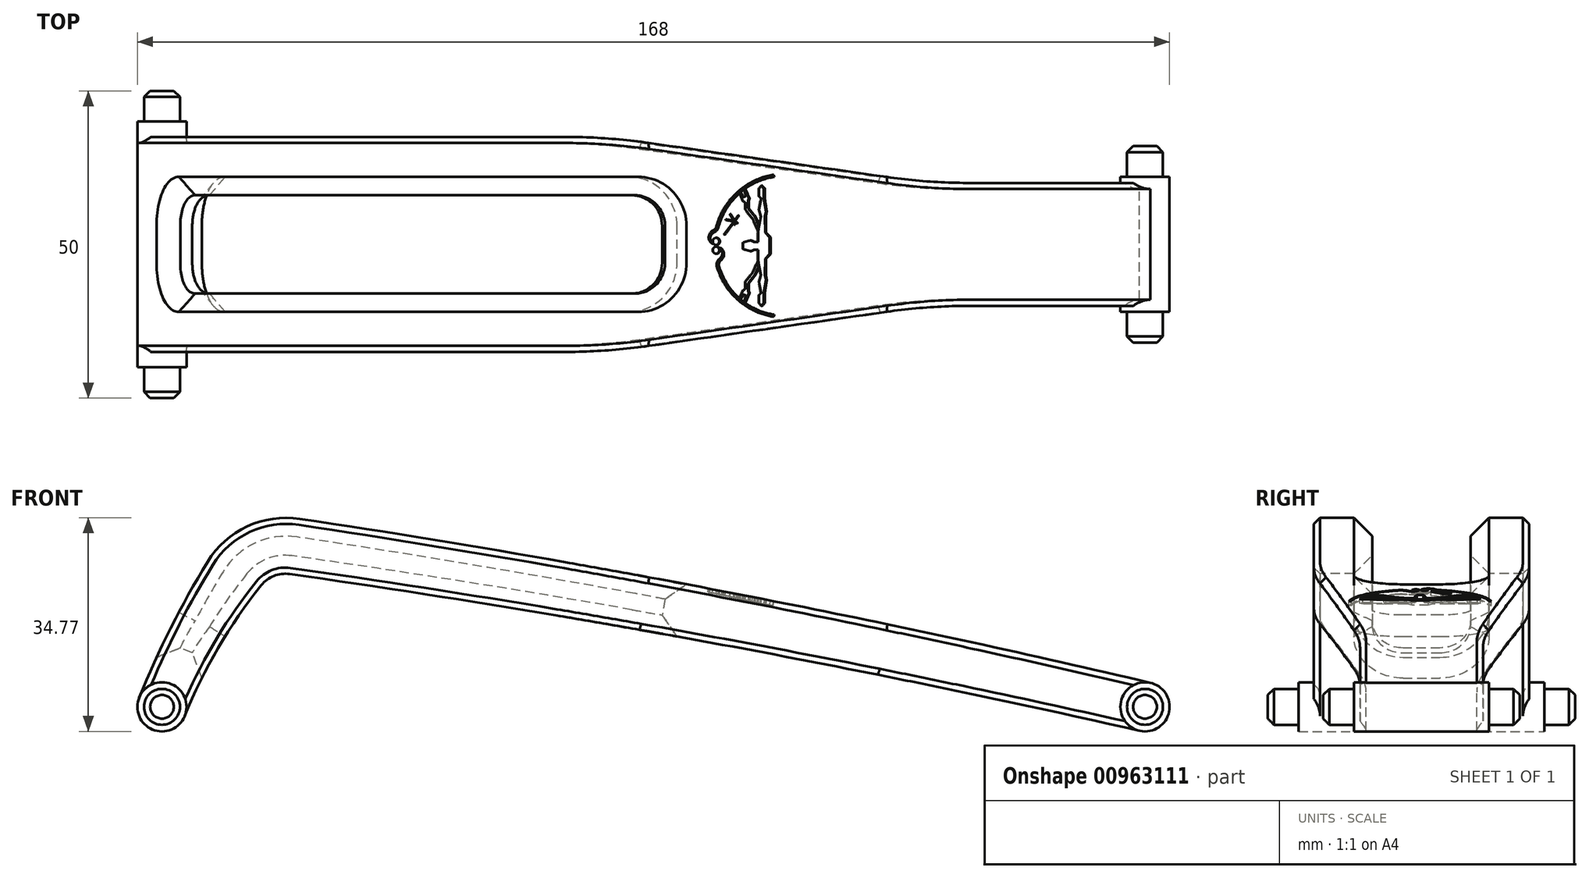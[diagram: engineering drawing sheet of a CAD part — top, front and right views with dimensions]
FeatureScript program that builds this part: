
annotation { "Feature Type Name" : "Feature", "Feature Type Description" : "" }
export const myFeature = defineFeature(function(context is Context, id is Id, definition is map)
    precondition{}
    {
        {
            var Q0;
            Q0=qCreatedBy(makeId("Front.planeOp"),FACE);
            var sketch = newSketch(context, id + "F0", { "sketchPlane" : qUnion([Q0])});
            skCircle(sketch, "E0", {"center": v(0, 0) * mm, "radius": 2.93 * mm});
            skSolve(sketch);
        }
        {
            var Q0;
            Q0 = qSketchRegion(id + "F0", true);
            extrude(context, id + "F1", {"entities" : qUnion([Q0]), "depth" : (22 + 10) * mm, "offsetDistance" : 25 * mm, "symmetric" : true});
        }
        {
            var Q0;
            Q0=qCreatedBy(makeId("Front.planeOp"),FACE);
            var sketch = newSketch(context, id + "F2", { "sketchPlane" : qUnion([Q0])});
            skCircle(sketch, "E1", {"center": v(-160, 0) * mm, "radius": 2.93 * mm});
            skSolve(sketch);
        }
        {
            var Q0;
            Q0 = qSketchRegion(id + "F2", true);
            extrude(context, id + "F3", {"entities" : qUnion([Q0]), "depth" : 50 * mm, "offsetDistance" : 25 * mm, "symmetric" : true});
        }
        {
            var Q0;
            Q0=qCreatedBy(makeId("Front.planeOp"),FACE);
            var sketch = newSketch(context, id + "F4", { "sketchPlane" : qUnion([Q0])});
            skCircle(sketch, "E2", {"center": v(0, 0) * mm, "radius": 4 * mm});
            skSolve(sketch);
        }
        {
            var Q0;
            Q0 = qSketchRegion(id + "F4", true);
            extrude(context, id + "F5", {"entities" : qUnion([Q0]), "operationType" : NewBodyOperationType.ADD, "depth" : (32 - 3 - 7) * mm, "offsetDistance" : 25 * mm, "symmetric" : true});
        }
        {
            var Q0;
            Q0=qCreatedBy(makeId("Front.planeOp"),FACE);
            var sketch = newSketch(context, id + "F6", { "sketchPlane" : qUnion([Q0])});
            skCircle(sketch, "E3", {"center": v(-160, 0) * mm, "radius": 4 * mm});
            skSolve(sketch);
        }
        {
            var Q0;
            Q0 = qSketchRegion(id + "F6", true);
            extrude(context, id + "F7", {"entities" : qUnion([Q0]), "operationType" : NewBodyOperationType.ADD, "depth" : (50 - 3 - 7) * mm, "offsetDistance" : 25 * mm, "symmetric" : true});
        }
        {
            var Q0;
            Q0=qCreatedBy(makeId("Front.planeOp"),FACE);
            var sketch = newSketch(context, id + "F8", { "sketchPlane" : qUnion([Q0])});
            skLineSegment(sketch, "E4", {"start": v(-0.83, -3.91) * mm, "end": v(0.83, 3.91) * mm});
            skLineSegment(sketch, "E5", {"start": v(0.83, 3.91) * mm, "end": v(-149.8, 35.93) * mm, "construction": true});
            skLineSegment(sketch, "E6", {"start": v(-163.7, 1.5) * mm, "end": v(-149.8, 35.93) * mm, "construction": true});
            skLineSegment(sketch, "E7", {"start": v(-156.3, -1.5) * mm, "end": v(-163.7, 1.5) * mm});
            skLineSegment(sketch, "E8", {"start": v(-144.9, 26.7) * mm, "end": v(-156.3, -1.5) * mm, "construction": true});
            skLineSegment(sketch, "E9", {"start": v(-144.9, 26.7) * mm, "end": v(-0.83, -3.91) * mm, "construction": true});
            skPoint(sketch, "E10", {"position": v(-160, 0) * mm});
            skLineSegment(sketch, "E11", {"start": v(-160, 0) * mm, "end": v(0, 0) * mm, "construction": true});
            skArc(sketch, "E12", {"start": v(-142, 22) * mm, "mid": v(-150.1, 10.83) * mm, "end": v(-156.3, -1.5) * mm});
            skArc(sketch, "E13", {"start": v(-0.83, -3.91) * mm, "mid": v(-71.14, 10.53) * mm, "end": v(-142, 22) * mm});
            skArc(sketch, "E14", {"start": v(-147.04, 32) * mm, "mid": v(-156.26, 17.23) * mm, "end": v(-163.7, 1.5) * mm});
            skArc(sketch, "E15", {"start": v(0.83, 3.91) * mm, "mid": v(-72.8, 19.6) * mm, "end": v(-147.04, 32) * mm});
            skSolve(sketch);
        }
        {
            var Q0;
            Q0 = qSketchRegion(id + "F8", true);
            extrude(context, id + "F9", {"entities" : qUnion([Q0]), "depth" : 20 * mm, "offsetDistance" : 25 * mm, "symmetric" : true});
        }
        {
            var Q0;
            Q0=makeQuery(id+"F9.opExtrude","SWEPT_BODY",BODY,{"disambiguationData":[OSD([sQuery(id+"F8.wireOp",EDGE,"E4"),sQuery(id+"F8.wireOp",EDGE,"E5"),sQuery(id+"F8.wireOp",EDGE,"E6"),sQuery(id+"F8.wireOp",EDGE,"E7"),sQuery(id+"F8.wireOp",EDGE,"E8"),sQuery(id+"F8.wireOp",EDGE,"E9")])]});
            var Q1;
            Q1=makeQuery(id+"F3.opExtrude","SWEPT_BODY",BODY,{"disambiguationData":[OSD([sQuery(id+"F2.wireOp",EDGE,"E1")])]});
            var Q2;
            Q2=makeQuery(id+"F1.opExtrude","SWEPT_BODY",BODY,{"disambiguationData":[OSD([sQuery(id+"F0.wireOp",EDGE,"E0")])]});
            booleanBodies(context, id + "F10", {"operationType" : BooleanOperationType.UNION, "tools" : qUnion([Q0, Q1, Q2])});
        }
        {
            var Q0;
            Q0=qCreatedBy(makeId("Front.planeOp"),FACE);
            var sketch = newSketch(context, id + "F11", { "sketchPlane" : qUnion([Q0])});
            skLineSegment(sketch, "E16", {"start": v(-163.7, 1.5) * mm, "end": v(-156.3, -1.5) * mm});
            skLineSegment(sketch, "E17", {"start": v(-88.98, 13.71) * mm, "end": v(-87.43, 22.3) * mm});
            skLineSegment(sketch, "E18", {"start": v(-87.43, 22.3) * mm, "end": v(-187.46, 40.4) * mm, "construction": true});
            skArc(sketch, "E19.0", {"start": v(-87.43, 22.3) * mm, "mid": v(-117.2, 27.42) * mm, "end": v(-147.04, 32) * mm});
            skArc(sketch, "E19.1", {"start": v(-88.98, 13.71) * mm, "mid": v(-115.46, 18.06) * mm, "end": v(-142, 22) * mm});
            skArc(sketch, "E19.2", {"start": v(-142, 22) * mm, "mid": v(-150.1, 10.83) * mm, "end": v(-156.3, -1.5) * mm});
            skArc(sketch, "E19.3", {"start": v(-147.04, 32) * mm, "mid": v(-156.26, 17.23) * mm, "end": v(-163.7, 1.5) * mm});
            skPoint(sketch, "E20.orphan", {"position": v(0.83, 3.91) * mm});
            skPoint(sketch, "E21.orphan", {"position": v(-0.94, -3.89) * mm});
            skSolve(sketch);
        }
        {
            var Q0;
            Q0 = qSketchRegion(id + "F11", true);
            extrude(context, id + "F12", {"entities" : qUnion([Q0]), "operationType" : NewBodyOperationType.ADD, "depth" : 35 * mm, "offsetDistance" : 25 * mm, "symmetric" : true});
        }
        {
            var Q0;
            Q0=makeQuery(id+"F12.boolean.opBoolean","INTERSECT",EDGE,{"derivedFrom":[makeQuery(id+"F9.opExtrude","CAP_FACE",FACE,{"disambiguationData":[OSD([sQuery(id+"F8.wireOp",EDGE,"E4"),sQuery(id+"F8.wireOp",EDGE,"E5"),sQuery(id+"F8.wireOp",EDGE,"E6"),sQuery(id+"F8.wireOp",EDGE,"E7"),sQuery(id+"F8.wireOp",EDGE,"E8"),sQuery(id+"F8.wireOp",EDGE,"E9")])],"isStart":true}),makeQuery(id+"F12.opExtrude","SWEPT_FACE",FACE,{"disambiguationData":[OSD([sQuery(id+"F11.wireOp",EDGE,"E17")])]})]});
            chamfer(context, id + "F13", {"entities" : qUnion([Q0]), "chamferType" : ChamferType.OFFSET_ANGLE, "width" : 7.5 * mm, "oppositeDirection" : false, "angle" : 82 * degree, "tangentPropagation" : true});
        }
        {
            var Q0;
            Q0=makeQuery(id+"F12.boolean.opBoolean","INTERSECT",EDGE,{"derivedFrom":[makeQuery(id+"F9.opExtrude","CAP_FACE",FACE,{"disambiguationData":[OSD([sQuery(id+"F8.wireOp",EDGE,"E4"),sQuery(id+"F8.wireOp",EDGE,"E5"),sQuery(id+"F8.wireOp",EDGE,"E6"),sQuery(id+"F8.wireOp",EDGE,"E7"),sQuery(id+"F8.wireOp",EDGE,"E8"),sQuery(id+"F8.wireOp",EDGE,"E9")])],"isStart":false}),makeQuery(id+"F12.opExtrude","SWEPT_FACE",FACE,{"disambiguationData":[OSD([sQuery(id+"F11.wireOp",EDGE,"E17")])]})]});
            chamfer(context, id + "F14", {"entities" : qUnion([Q0]), "chamferType" : ChamferType.OFFSET_ANGLE, "width" : 7.5 * mm, "oppositeDirection" : true, "angle" : 82 * degree, "tangentPropagation" : true});
        }
        {
            var Q0;
            {var subQ0=makeQuery(id+"F9.opExtrude","CAP_FACE",FACE,{"disambiguationData":[OSD([sQuery(id+"F8.wireOp",EDGE,"E4"),sQuery(id+"F8.wireOp",EDGE,"E5"),sQuery(id+"F8.wireOp",EDGE,"E6"),sQuery(id+"F8.wireOp",EDGE,"E7"),sQuery(id+"F8.wireOp",EDGE,"E8"),sQuery(id+"F8.wireOp",EDGE,"E9")])],"isStart":true});Q0=makeQuery(id+"F13.opChamfer","BLEND_EDGE",EDGE,{"blendedFrom":[makeQuery(id+"F12.boolean.opBoolean","INTERSECT",EDGE,{"derivedFrom":[subQ0,makeQuery(id+"F12.opExtrude","SWEPT_FACE",FACE,{"disambiguationData":[OSD([sQuery(id+"F11.wireOp",EDGE,"E17")])]})]}),subQ0],"blendedInto":[subQ0]});}
            var Q1;
            {var subQ0=sQuery(id+"F11.wireOp",EDGE,"E17");Q1=makeQuery(id+"F13.opChamfer","BLEND_EDGE",EDGE,{"blendedFrom":[makeQuery(id+"F12.boolean.opBoolean","INTERSECT",EDGE,{"derivedFrom":[makeQuery(id+"F9.opExtrude","CAP_FACE",FACE,{"disambiguationData":[OSD([sQuery(id+"F8.wireOp",EDGE,"E4"),sQuery(id+"F8.wireOp",EDGE,"E5"),sQuery(id+"F8.wireOp",EDGE,"E6"),sQuery(id+"F8.wireOp",EDGE,"E7"),sQuery(id+"F8.wireOp",EDGE,"E8"),sQuery(id+"F8.wireOp",EDGE,"E9")])],"isStart":true}),makeQuery(id+"F12.opExtrude","SWEPT_FACE",FACE,{"disambiguationData":[OSD([subQ0])]})]}),makeQuery(id+"F12.opExtrude","CAP_FACE",FACE,{"disambiguationData":[OSD([sQuery(id+"F11.wireOp",EDGE,"2c269e23-bd51-4eb5-b0e0-de77504a2cef.0"),sQuery(id+"F11.wireOp",EDGE,"2c269e23-bd51-4eb5-b0e0-de77504a2cef.2"),sQuery(id+"F11.wireOp",EDGE,"2c269e23-bd51-4eb5-b0e0-de77504a2cef.3"),sQuery(id+"F11.wireOp",EDGE,"2c269e23-bd51-4eb5-b0e0-de77504a2cef.4"),sQuery(id+"F11.wireOp",EDGE,"E16"),subQ0])],"isStart":true})],"blendedInto":[makeQuery(id+"F12.opExtrude","CAP_FACE",FACE,{"disambiguationData":[OSD([sQuery(id+"F11.wireOp",EDGE,"2c269e23-bd51-4eb5-b0e0-de77504a2cef.0"),sQuery(id+"F11.wireOp",EDGE,"2c269e23-bd51-4eb5-b0e0-de77504a2cef.2"),sQuery(id+"F11.wireOp",EDGE,"2c269e23-bd51-4eb5-b0e0-de77504a2cef.3"),sQuery(id+"F11.wireOp",EDGE,"2c269e23-bd51-4eb5-b0e0-de77504a2cef.4"),sQuery(id+"F11.wireOp",EDGE,"E16"),subQ0])],"isStart":true})]});}
            var Q2;
            {var subQ0=sQuery(id+"F11.wireOp",EDGE,"E17");Q2=makeQuery(id+"F14.opChamfer","BLEND_EDGE",EDGE,{"blendedFrom":[makeQuery(id+"F12.boolean.opBoolean","INTERSECT",EDGE,{"derivedFrom":[makeQuery(id+"F9.opExtrude","CAP_FACE",FACE,{"disambiguationData":[OSD([sQuery(id+"F8.wireOp",EDGE,"E4"),sQuery(id+"F8.wireOp",EDGE,"E5"),sQuery(id+"F8.wireOp",EDGE,"E6"),sQuery(id+"F8.wireOp",EDGE,"E7"),sQuery(id+"F8.wireOp",EDGE,"E8"),sQuery(id+"F8.wireOp",EDGE,"E9")])],"isStart":false}),makeQuery(id+"F12.opExtrude","SWEPT_FACE",FACE,{"disambiguationData":[OSD([subQ0])]})]}),makeQuery(id+"F12.opExtrude","CAP_FACE",FACE,{"disambiguationData":[OSD([sQuery(id+"F11.wireOp",EDGE,"2c269e23-bd51-4eb5-b0e0-de77504a2cef.0"),sQuery(id+"F11.wireOp",EDGE,"2c269e23-bd51-4eb5-b0e0-de77504a2cef.2"),sQuery(id+"F11.wireOp",EDGE,"2c269e23-bd51-4eb5-b0e0-de77504a2cef.3"),sQuery(id+"F11.wireOp",EDGE,"2c269e23-bd51-4eb5-b0e0-de77504a2cef.4"),sQuery(id+"F11.wireOp",EDGE,"E16"),subQ0])],"isStart":false})],"blendedInto":[makeQuery(id+"F12.opExtrude","CAP_FACE",FACE,{"disambiguationData":[OSD([sQuery(id+"F11.wireOp",EDGE,"2c269e23-bd51-4eb5-b0e0-de77504a2cef.0"),sQuery(id+"F11.wireOp",EDGE,"2c269e23-bd51-4eb5-b0e0-de77504a2cef.2"),sQuery(id+"F11.wireOp",EDGE,"2c269e23-bd51-4eb5-b0e0-de77504a2cef.3"),sQuery(id+"F11.wireOp",EDGE,"2c269e23-bd51-4eb5-b0e0-de77504a2cef.4"),sQuery(id+"F11.wireOp",EDGE,"E16"),subQ0])],"isStart":false})]});}
            var Q3;
            {var subQ0=makeQuery(id+"F9.opExtrude","CAP_FACE",FACE,{"disambiguationData":[OSD([sQuery(id+"F8.wireOp",EDGE,"E4"),sQuery(id+"F8.wireOp",EDGE,"E5"),sQuery(id+"F8.wireOp",EDGE,"E6"),sQuery(id+"F8.wireOp",EDGE,"E7"),sQuery(id+"F8.wireOp",EDGE,"E8"),sQuery(id+"F8.wireOp",EDGE,"E9")])],"isStart":false});Q3=makeQuery(id+"F14.opChamfer","BLEND_EDGE",EDGE,{"blendedFrom":[makeQuery(id+"F12.boolean.opBoolean","INTERSECT",EDGE,{"derivedFrom":[subQ0,makeQuery(id+"F12.opExtrude","SWEPT_FACE",FACE,{"disambiguationData":[OSD([sQuery(id+"F11.wireOp",EDGE,"E17")])]})]}),subQ0],"blendedInto":[subQ0]});}
            fillet(context, id + "F15", {"entities" : qUnion([Q0, Q1, Q2, Q3]), "radius" : 100 * mm, "tangentPropagation" : true, "allowEdgeOverflow" : false});
        }
        {
            var Q0;
            Q0=qCreatedBy(makeId("Front.planeOp"),FACE);
            var sketch = newSketch(context, id + "F16", { "sketchPlane" : qUnion([Q0])});
            skLineSegment(sketch, "E22", {"start": v(-145.4, 4.89) * mm, "end": v(-167.02, 13.62) * mm});
            skLineSegment(sketch, "E23", {"start": v(-76.52, 26.4) * mm, "end": v(-80.63, 3.67) * mm});
            skPoint(sketch, "E24", {"position": v(-160, 0) * mm});
            skArc(sketch, "E25", {"start": v(-76.52, 26.4) * mm, "mid": v(-126.34, 52.33) * mm, "end": v(-167.02, 13.62) * mm});
            skArc(sketch, "E26", {"start": v(-80.63, 3.67) * mm, "mid": v(-112.95, 7.88) * mm, "end": v(-145.4, 4.89) * mm});
            skSolve(sketch);
        }
        {
            var Q0;
            Q0 = qSketchRegion(id + "F16", true);
            extrude(context, id + "F17", {"entities" : qUnion([Q0]), "operationType" : NewBodyOperationType.REMOVE, "oppositeDirection" : true, "depth" : 16 * mm, "offsetDistance" : 25 * mm, "symmetric" : true});
        }
        {
            var Q0;
            Q0=makeQuery(id+"F17.boolean.opBoolean","COPY",EDGE,{"derivedFrom":makeQuery(id+"F17.opExtrude","CAP_EDGE",EDGE,{"disambiguationData":[OSD([sQuery(id+"F16.wireOp",EDGE,"E22")])],"isStart":false})});
            var Q1;
            Q1=makeQuery(id+"F17.boolean.opBoolean","COPY",EDGE,{"derivedFrom":makeQuery(id+"F17.opExtrude","CAP_EDGE",EDGE,{"disambiguationData":[OSD([sQuery(id+"F16.wireOp",EDGE,"E22")])],"isStart":true})});
            var Q2;
            Q2=makeQuery(id+"F17.boolean.opBoolean","COPY",EDGE,{"derivedFrom":makeQuery(id+"F17.opExtrude","CAP_EDGE",EDGE,{"disambiguationData":[OSD([sQuery(id+"F16.wireOp",EDGE,"E23")])],"isStart":true})});
            var Q3;
            Q3=makeQuery(id+"F17.boolean.opBoolean","COPY",EDGE,{"derivedFrom":makeQuery(id+"F17.opExtrude","CAP_EDGE",EDGE,{"disambiguationData":[OSD([sQuery(id+"F16.wireOp",EDGE,"E23")])],"isStart":false})});
            fillet(context, id + "F18", {"entities" : qUnion([Q0, Q1, Q2, Q3]), "radius" : 5 * mm, "tangentPropagation" : true, "allowEdgeOverflow" : false});
        }
        {
            var Q0;
            {var subQ0=sQuery(id+"F11.wireOp",EDGE,"E19.2");var subQ1=sQuery(id+"F11.wireOp",EDGE,"E19.1");var subQ2=sQuery(id+"F8.wireOp",EDGE,"E13");var subQ3=sQuery(id+"F8.wireOp",EDGE,"E12");Q0=makeQuery(id+"F17.boolean.opBoolean","SPLIT",EDGE,{"disambiguationData":[TD([makeQuery(id+"F17.opExtrude","CAP_FACE",FACE,{"disambiguationData":[OSD([sQuery(id+"F16.wireOp",EDGE,"E22"),sQuery(id+"F16.wireOp",EDGE,"E23"),sQuery(id+"F16.wireOp",EDGE,"E25"),sQuery(id+"F16.wireOp",EDGE,"E26")])],"isStart":false})])],"derivedFrom":makeQuery(id+"F12.boolean.opBoolean","MERGE",EDGE,{"derivedFrom":[makeQuery(id+"F9.opExtrude","SWEPT_EDGE",EDGE,{"disambiguationData":[OSD([subQ3,subQ2])]}),makeQuery(id+"F12.opExtrude","SWEPT_EDGE",EDGE,{"disambiguationData":[OSD([subQ1,subQ0])]})]})});}
            var Q1;
            {var subQ0=sQuery(id+"F11.wireOp",EDGE,"E19.2");var subQ1=sQuery(id+"F11.wireOp",EDGE,"E19.1");var subQ2=sQuery(id+"F8.wireOp",EDGE,"E13");var subQ3=sQuery(id+"F8.wireOp",EDGE,"E12");Q1=makeQuery(id+"F17.boolean.opBoolean","SPLIT",EDGE,{"disambiguationData":[TD([makeQuery(id+"F17.opExtrude","CAP_FACE",FACE,{"disambiguationData":[OSD([sQuery(id+"F16.wireOp",EDGE,"E22"),sQuery(id+"F16.wireOp",EDGE,"E23"),sQuery(id+"F16.wireOp",EDGE,"E25"),sQuery(id+"F16.wireOp",EDGE,"E26")])],"isStart":true})])],"derivedFrom":makeQuery(id+"F12.boolean.opBoolean","MERGE",EDGE,{"derivedFrom":[makeQuery(id+"F9.opExtrude","SWEPT_EDGE",EDGE,{"disambiguationData":[OSD([subQ3,subQ2])]}),makeQuery(id+"F12.opExtrude","SWEPT_EDGE",EDGE,{"disambiguationData":[OSD([subQ1,subQ0])]})]})});}
            fillet(context, id + "F19", {"entities" : qUnion([Q0, Q1]), "tangentPropagation" : true, "radius" : 5 * mm, "defaultsChanged" : false, "vertexSettings" : [], "allowEdgeOverflow" : false});
        }
        {
            var Q0;
            {var subQ0=sQuery(id+"F11.wireOp",EDGE,"E19.0");var subQ1=sQuery(id+"F11.wireOp",EDGE,"E19.3");var subQ2=sQuery(id+"F8.wireOp",EDGE,"E14");var subQ3=sQuery(id+"F8.wireOp",EDGE,"E15");Q0=makeQuery(id+"F17.boolean.opBoolean","SPLIT",EDGE,{"disambiguationData":[TD([makeQuery(id+"F17.opExtrude","CAP_FACE",FACE,{"disambiguationData":[OSD([sQuery(id+"F16.wireOp",EDGE,"E22"),sQuery(id+"F16.wireOp",EDGE,"E23"),sQuery(id+"F16.wireOp",EDGE,"E25"),sQuery(id+"F16.wireOp",EDGE,"E26")])],"isStart":false})])],"derivedFrom":makeQuery(id+"F12.boolean.opBoolean","MERGE",EDGE,{"derivedFrom":[makeQuery(id+"F9.opExtrude","SWEPT_EDGE",EDGE,{"disambiguationData":[OSD([subQ2,subQ3])]}),makeQuery(id+"F12.opExtrude","SWEPT_EDGE",EDGE,{"disambiguationData":[OSD([subQ0,subQ1])]})]})});}
            var Q1;
            {var subQ0=sQuery(id+"F11.wireOp",EDGE,"E19.0");var subQ1=sQuery(id+"F8.wireOp",EDGE,"E15");var subQ2=sQuery(id+"F11.wireOp",EDGE,"E19.3");var subQ3=sQuery(id+"F8.wireOp",EDGE,"E14");Q1=makeQuery(id+"F17.boolean.opBoolean","SPLIT",EDGE,{"disambiguationData":[TD([makeQuery(id+"F17.opExtrude","CAP_FACE",FACE,{"disambiguationData":[OSD([sQuery(id+"F16.wireOp",EDGE,"E22"),sQuery(id+"F16.wireOp",EDGE,"E23"),sQuery(id+"F16.wireOp",EDGE,"E25"),sQuery(id+"F16.wireOp",EDGE,"E26")])],"isStart":true})])],"derivedFrom":makeQuery(id+"F12.boolean.opBoolean","MERGE",EDGE,{"derivedFrom":[makeQuery(id+"F9.opExtrude","SWEPT_EDGE",EDGE,{"disambiguationData":[OSD([subQ3,subQ1])]}),makeQuery(id+"F12.opExtrude","SWEPT_EDGE",EDGE,{"disambiguationData":[OSD([subQ0,subQ2])]})]})});}
            fillet(context, id + "F20", {"entities" : qUnion([Q0, Q1]), "tangentPropagation" : true, "radius" : 15 * mm, "defaultsChanged" : true, "vertexSettings" : [], "allowEdgeOverflow" : false});
        }
        {
            var Q0;
            Q0=makeQuery(id+"F12.opExtrude","CAP_EDGE",EDGE,{"disambiguationData":[OSD([sQuery(id+"F11.wireOp",EDGE,"2c269e23-bd51-4eb5-b0e0-de77504a2cef.4")])],"isStart":false});
            var Q1;
            Q1=makeQuery(id+"F12.opExtrude","CAP_EDGE",EDGE,{"disambiguationData":[OSD([sQuery(id+"F11.wireOp",EDGE,"2c269e23-bd51-4eb5-b0e0-de77504a2cef.4")])],"isStart":true});
            var Q2;
            Q2=makeQuery(id+"F17.boolean.opBoolean","INTERSECT",EDGE,{"derivedFrom":[makeQuery(id+"F12.boolean.opBoolean","MERGE",FACE,{"derivedFrom":[makeQuery(id+"F9.opExtrude","SWEPT_FACE",FACE,{"disambiguationData":[OSD([sQuery(id+"F8.wireOp",EDGE,"E13")])]}),makeQuery(id+"F12.opExtrude","SWEPT_FACE",FACE,{"disambiguationData":[OSD([sQuery(id+"F11.wireOp",EDGE,"E19.1")])]})]}),makeQuery(id+"F17.opExtrude","CAP_FACE",FACE,{"disambiguationData":[OSD([sQuery(id+"F16.wireOp",EDGE,"E22"),sQuery(id+"F16.wireOp",EDGE,"E23"),sQuery(id+"F16.wireOp",EDGE,"E25"),sQuery(id+"F16.wireOp",EDGE,"E26")])],"isStart":false})]});
            var Q3;
            Q3=makeQuery(id+"F17.boolean.opBoolean","INTERSECT",EDGE,{"derivedFrom":[makeQuery(id+"F12.boolean.opBoolean","MERGE",FACE,{"derivedFrom":[makeQuery(id+"F9.opExtrude","SWEPT_FACE",FACE,{"disambiguationData":[OSD([sQuery(id+"F8.wireOp",EDGE,"E15")])]}),makeQuery(id+"F12.opExtrude","SWEPT_FACE",FACE,{"disambiguationData":[OSD([sQuery(id+"F11.wireOp",EDGE,"E19.0")])]})]}),makeQuery(id+"F17.opExtrude","CAP_FACE",FACE,{"disambiguationData":[OSD([sQuery(id+"F16.wireOp",EDGE,"E22"),sQuery(id+"F16.wireOp",EDGE,"E23"),sQuery(id+"F16.wireOp",EDGE,"E25"),sQuery(id+"F16.wireOp",EDGE,"E26")])],"isStart":false})]});
            chamfer(context, id + "F21", {"entities" : qUnion([Q0, Q1, Q2, Q3]), "width" : 3 * mm, "tangentPropagation" : true});
        }
        {
            var Q0;
            Q0=makeQuery(id+"F12.opExtrude","CAP_EDGE",EDGE,{"disambiguationData":[OSD([sQuery(id+"F11.wireOp",EDGE,"2c269e23-bd51-4eb5-b0e0-de77504a2cef.0")])],"isStart":false});
            var Q1;
            Q1=makeQuery(id+"F12.opExtrude","CAP_EDGE",EDGE,{"disambiguationData":[OSD([sQuery(id+"F11.wireOp",EDGE,"2c269e23-bd51-4eb5-b0e0-de77504a2cef.0")])],"isStart":true});
            var Q2;
            Q2=makeQuery(id+"F12.opExtrude","CAP_EDGE",EDGE,{"disambiguationData":[OSD([sQuery(id+"F11.wireOp",EDGE,"E19.0")])],"isStart":false});
            var Q3;
            Q3=makeQuery(id+"F12.opExtrude","CAP_EDGE",EDGE,{"disambiguationData":[OSD([sQuery(id+"F11.wireOp",EDGE,"E19.0")])],"isStart":true});
            var Q4;
            Q4=makeQuery(id+"F12.opExtrude","CAP_EDGE",EDGE,{"disambiguationData":[OSD([sQuery(id+"F11.wireOp",EDGE,"E19.1")])],"isStart":false});
            var Q5;
            Q5=makeQuery(id+"F12.opExtrude","CAP_EDGE",EDGE,{"disambiguationData":[OSD([sQuery(id+"F11.wireOp",EDGE,"E19.1")])],"isStart":true});
            chamfer(context, id + "F22", {"entities" : qUnion([Q0, Q1, Q2, Q3, Q4, Q5]), "width" : 1 * mm, "tangentPropagation" : true});
        }
        {
            var Q0;
            Q0=makeQuery(id+"F3.opExtrude","CAP_EDGE",EDGE,{"disambiguationData":[OSD([sQuery(id+"F2.wireOp",EDGE,"E1")])],"isStart":false});
            var Q1;
            Q1=makeQuery(id+"F1.opExtrude","CAP_EDGE",EDGE,{"disambiguationData":[OSD([sQuery(id+"F0.wireOp",EDGE,"E0")])],"isStart":false});
            var Q2;
            Q2=makeQuery(id+"F1.opExtrude","CAP_EDGE",EDGE,{"disambiguationData":[OSD([sQuery(id+"F0.wireOp",EDGE,"E0")])],"isStart":true});
            var Q3;
            Q3=makeQuery(id+"F3.opExtrude","CAP_EDGE",EDGE,{"disambiguationData":[OSD([sQuery(id+"F2.wireOp",EDGE,"E1")])],"isStart":true});
            chamfer(context, id + "F23", {"entities" : qUnion([Q0, Q1, Q2, Q3]), "width" : 1 * mm, "tangentPropagation" : true});
        }
        {
            var Q0;
            Q0=qCreatedBy(makeId("Top.planeOp"),FACE);
            var Q1;
            Q1=makeQuery(id+"F5.opExtrude","SWEPT_FACE",FACE,{"disambiguationData":[OSD([sQuery(id+"F4.wireOp",EDGE,"E2")])]});
            cPlane(context, id + "F24", {"entities" : qUnion([Q0, Q1]), "cplaneType" : CPlaneType.LINE_ANGLE, "offset" : 25 * mm, "angle" : 12 * degree, "width" : 150 * mm, "height" : 150 * mm});
        }
        {
            var Q0;
            Q0=qCreatedBy(id+"F24.planeOp",FACE);
            cPlane(context, id + "F25", {"entities" : qUnion([Q0]), "cplaneType" : CPlaneType.OFFSET, "offset" : 10 * mm, "oppositeDirection" : true, "width" : 150 * mm, "height" : 150 * mm});
        }
        {
            var Q0;
            Q0=qCreatedBy(id+"F25.planeOp",FACE);
            var sketch = newSketch(context, id + "F26", { "sketchPlane" : qUnion([Q0])});
            skLineSegment(sketch, "E27", {"start": v(-67.75, -7) * mm, "end": v(-68.51, -8.7) * mm});
            skLineSegment(sketch, "E28", {"start": v(-67.4, -6.86) * mm, "end": v(-67.75, -7) * mm});
            skLineSegment(sketch, "E29", {"start": v(-67.4, -5.66) * mm, "end": v(-67.4, -6.86) * mm});
            skLineSegment(sketch, "E30", {"start": v(-66.15, -4.12) * mm, "end": v(-67.4, -5.66) * mm});
            skLineSegment(sketch, "E31", {"start": v(-65.32, -2.25) * mm, "end": v(-66.15, -4.12) * mm});
            skLineSegment(sketch, "E32", {"start": v(-65.12, -3.26) * mm, "end": v(-65.32, -2.25) * mm});
            skLineSegment(sketch, "E33", {"start": v(-65.64, -4.43) * mm, "end": v(-65.12, -3.26) * mm});
            skLineSegment(sketch, "E34", {"start": v(-66.8, -5.87) * mm, "end": v(-65.64, -4.43) * mm});
            skLineSegment(sketch, "E35", {"start": v(-66.8, -7.12) * mm, "end": v(-66.8, -5.87) * mm});
            skLineSegment(sketch, "E36", {"start": v(-66.67, -7.48) * mm, "end": v(-66.8, -7.12) * mm});
            skLineSegment(sketch, "E37", {"start": v(-67.38, -9.07) * mm, "end": v(-66.67, -7.48) * mm});
            skLineSegment(sketch, "E38", {"start": v(-67.55, -8.94) * mm, "end": v(-67.38, -9.07) * mm});
            skLineSegment(sketch, "E39", {"start": v(-67.28, -7.88) * mm, "end": v(-67.55, -8.94) * mm});
            skLineSegment(sketch, "E40", {"start": v(-67.64, -7.72) * mm, "end": v(-67.28, -7.88) * mm});
            skLineSegment(sketch, "E41", {"start": v(-68.35, -8.77) * mm, "end": v(-67.64, -7.72) * mm});
            skLineSegment(sketch, "E42", {"start": v(-68.51, -8.7) * mm, "end": v(-68.35, -8.77) * mm});
            skLineSegment(sketch, "E43", {"start": v(-68.12, -8.53) * mm, "end": v(-68.32, -8.83) * mm});
            skArc(sketch, "E44", {"start": v(-68.12, -8.53) * mm, "mid": v(-65.53, -10.14) * mm, "end": v(-62.62, -11) * mm});
            skLineSegment(sketch, "E45", {"start": v(-62.67, -11.35) * mm, "end": v(-62.62, -11) * mm});
            skArc(sketch, "E46", {"start": v(-68.32, -8.83) * mm, "mid": v(-65.67, -10.47) * mm, "end": v(-62.67, -11.35) * mm});
            skLineSegment(sketch, "E47", {"start": v(-67.77, 0.77) * mm, "end": v(-67.77, -0.32) * mm});
            skLineSegment(sketch, "E48", {"start": v(-66.47, 1.12) * mm, "end": v(-67.77, 0.77) * mm});
            skLineSegment(sketch, "E49", {"start": v(-65.85, 0.87) * mm, "end": v(-66.47, 1.12) * mm});
            skLineSegment(sketch, "E50", {"start": v(-65.29, 0.87) * mm, "end": v(-65.85, 0.87) * mm});
            skLineSegment(sketch, "E51", {"start": v(-65.29, 2.5) * mm, "end": v(-65.29, 0.87) * mm});
            skLineSegment(sketch, "E52", {"start": v(-64.8, 4.98) * mm, "end": v(-65.29, 2.5) * mm});
            skLineSegment(sketch, "E53", {"start": v(-65.11, 6.1) * mm, "end": v(-64.8, 4.98) * mm});
            skLineSegment(sketch, "E54", {"start": v(-64.76, 7.94) * mm, "end": v(-65.11, 6.1) * mm});
            skLineSegment(sketch, "E55", {"start": v(-65.11, 8.24) * mm, "end": v(-64.76, 7.94) * mm});
            skLineSegment(sketch, "E56", {"start": v(-65.11, 9.54) * mm, "end": v(-65.11, 8.24) * mm});
            skLineSegment(sketch, "E57", {"start": v(-64.66, 10.06) * mm, "end": v(-65.11, 9.54) * mm});
            skLineSegment(sketch, "E58", {"start": v(-64.17, 9.56) * mm, "end": v(-64.66, 10.06) * mm});
            skLineSegment(sketch, "E59", {"start": v(-64.17, 7.94) * mm, "end": v(-64.17, 9.56) * mm});
            skLineSegment(sketch, "E60", {"start": v(-63.83, 5.79) * mm, "end": v(-64.17, 7.94) * mm});
            skLineSegment(sketch, "E61", {"start": v(-64, 4.95) * mm, "end": v(-63.83, 5.79) * mm});
            skLineSegment(sketch, "E62", {"start": v(-63.95, 2.35) * mm, "end": v(-64, 4.95) * mm});
            skLineSegment(sketch, "E63", {"start": v(-63.21, 1.6) * mm, "end": v(-63.95, 2.35) * mm});
            skLineSegment(sketch, "E64", {"start": v(-63.21, -1.16) * mm, "end": v(-63.21, 1.6) * mm});
            skLineSegment(sketch, "E65", {"start": v(-63.95, -1.9) * mm, "end": v(-63.21, -1.16) * mm});
            skLineSegment(sketch, "E66", {"start": v(-64, -4.5) * mm, "end": v(-63.95, -1.9) * mm});
            skLineSegment(sketch, "E67", {"start": v(-63.83, -5.34) * mm, "end": v(-64, -4.5) * mm});
            skLineSegment(sketch, "E68", {"start": v(-64.17, -7.5) * mm, "end": v(-63.83, -5.34) * mm});
            skLineSegment(sketch, "E69", {"start": v(-64.17, -9.12) * mm, "end": v(-64.17, -7.5) * mm});
            skLineSegment(sketch, "E70", {"start": v(-64.66, -9.62) * mm, "end": v(-64.17, -9.12) * mm});
            skLineSegment(sketch, "E71", {"start": v(-65.11, -9.09) * mm, "end": v(-64.66, -9.62) * mm});
            skLineSegment(sketch, "E72", {"start": v(-65.11, -7.8) * mm, "end": v(-65.11, -9.09) * mm});
            skLineSegment(sketch, "E73", {"start": v(-64.76, -7.5) * mm, "end": v(-65.11, -7.8) * mm});
            skLineSegment(sketch, "E74", {"start": v(-65.11, -5.66) * mm, "end": v(-64.76, -7.5) * mm});
            skLineSegment(sketch, "E75", {"start": v(-64.8, -4.53) * mm, "end": v(-65.11, -5.66) * mm});
            skLineSegment(sketch, "E76", {"start": v(-65.29, -2.05) * mm, "end": v(-64.8, -4.53) * mm});
            skLineSegment(sketch, "E77", {"start": v(-65.29, -0.42) * mm, "end": v(-65.29, -2.05) * mm});
            skLineSegment(sketch, "E78", {"start": v(-65.85, -0.42) * mm, "end": v(-65.29, -0.42) * mm});
            skLineSegment(sketch, "E79", {"start": v(-66.47, -0.68) * mm, "end": v(-65.85, -0.42) * mm});
            skLineSegment(sketch, "E80", {"start": v(-67.77, -0.32) * mm, "end": v(-66.47, -0.68) * mm});
            skArc(sketch, "E81", {"start": v(-67.7, 9.76) * mm, "mid": v(-70.38, 7.1) * mm, "end": v(-72.08, 3.71) * mm});
            skLineSegment(sketch, "E82", {"start": v(-67.6, 9.4) * mm, "end": v(-67.7, 9.76) * mm});
            skArc(sketch, "E83", {"start": v(-67.6, 9.4) * mm, "mid": v(-70.13, 6.83) * mm, "end": v(-71.74, 3.6) * mm});
            skArc(sketch, "E84", {"start": v(-71.74, 3.6) * mm, "mid": v(-71.74, 3.04) * mm, "end": v(-71.4, 2.57) * mm});
            skArc(sketch, "E85", {"start": v(-71.6, 0.5) * mm, "mid": v(-70.93, 1.48) * mm, "end": v(-71.4, 2.57) * mm});
            skLineSegment(sketch, "E86", {"start": v(-71.66, 0.6) * mm, "end": v(-71.6, 0.5) * mm});
            skArc(sketch, "E87", {"start": v(-71.66, 0.6) * mm, "mid": v(-71.2, 1.43) * mm, "end": v(-71.62, 2.28) * mm});
            skArc(sketch, "E88", {"start": v(-72.08, 3.71) * mm, "mid": v(-72.08, 2.93) * mm, "end": v(-71.62, 2.28) * mm});
            skCircle(sketch, "E89", {"center": v(-72.2, 0.94) * mm, "radius": 0.6 * mm});
            skLineSegment(sketch, "E90", {"start": v(-66.8, 7.57) * mm, "end": v(-66.67, 7.92) * mm});
            skLineSegment(sketch, "E91", {"start": v(-66.8, 6.32) * mm, "end": v(-66.8, 7.57) * mm});
            skLineSegment(sketch, "E92", {"start": v(-65.64, 4.88) * mm, "end": v(-66.8, 6.32) * mm});
            skLineSegment(sketch, "E93", {"start": v(-65.13, 3.74) * mm, "end": v(-65.64, 4.88) * mm});
            skLineSegment(sketch, "E94", {"start": v(-65.33, 2.72) * mm, "end": v(-65.13, 3.74) * mm});
            skLineSegment(sketch, "E95", {"start": v(-67.4, 6.1) * mm, "end": v(-66.15, 4.57) * mm});
            skLineSegment(sketch, "E96", {"start": v(-67.4, 7.3) * mm, "end": v(-67.4, 6.1) * mm});
            skLineSegment(sketch, "E97", {"start": v(-67.75, 7.44) * mm, "end": v(-67.4, 7.3) * mm});
            skLineSegment(sketch, "E98", {"start": v(-68.32, 8.72) * mm, "end": v(-67.75, 7.44) * mm});
            skLineSegment(sketch, "E99", {"start": v(-68.13, 8.9) * mm, "end": v(-68.32, 8.72) * mm});
            skLineSegment(sketch, "E100", {"start": v(-67.64, 8.17) * mm, "end": v(-68.13, 8.9) * mm});
            skLineSegment(sketch, "E101", {"start": v(-67.28, 8.33) * mm, "end": v(-67.64, 8.17) * mm});
            skLineSegment(sketch, "E102", {"start": v(-67.6, 9.56) * mm, "end": v(-67.28, 8.33) * mm});
            skLineSegment(sketch, "E103", {"start": v(-67.43, 9.63) * mm, "end": v(-67.6, 9.56) * mm});
            skLineSegment(sketch, "E104", {"start": v(-66.67, 7.92) * mm, "end": v(-67.43, 9.63) * mm});
            skLineSegment(sketch, "E105", {"start": v(-66.15, 4.57) * mm, "end": v(-65.33, 2.72) * mm});
            skLineSegment(sketch, "E106", {"start": v(-67.5, 9.9) * mm, "end": v(-67.34, 9.57) * mm});
            skArc(sketch, "E107", {"start": v(-62.67, 11.8) * mm, "mid": v(-65.19, 11.11) * mm, "end": v(-67.5, 9.9) * mm});
            skLineSegment(sketch, "E108", {"start": v(-62.62, 11.44) * mm, "end": v(-62.67, 11.8) * mm});
            skArc(sketch, "E109", {"start": v(-62.62, 11.44) * mm, "mid": v(-65.09, 10.77) * mm, "end": v(-67.34, 9.57) * mm});
            skLineSegment(sketch, "E110", {"start": v(-69.91, -4.88) * mm, "end": v(-69.81, -4.95) * mm});
            skLineSegment(sketch, "E111", {"start": v(-70.63, -4.07) * mm, "end": v(-69.28, -3.88) * mm});
            skLineSegment(sketch, "E112", {"start": v(-70.65, -3.95) * mm, "end": v(-70.63, -4.07) * mm});
            skLineSegment(sketch, "E113", {"start": v(-69.27, -3.76) * mm, "end": v(-70.65, -3.95) * mm});
            skLineSegment(sketch, "E114", {"start": v(-70.9, -1.6) * mm, "end": v(-69.27, -3.76) * mm});
            skLineSegment(sketch, "E115", {"start": v(-70.8, -1.53) * mm, "end": v(-70.9, -1.6) * mm});
            skLineSegment(sketch, "E116", {"start": v(-69.22, -3.63) * mm, "end": v(-70.8, -1.53) * mm});
            skLineSegment(sketch, "E117", {"start": v(-69.22, -3.18) * mm, "end": v(-69.22, -3.63) * mm});
            skLineSegment(sketch, "E118", {"start": v(-69.28, -3.88) * mm, "end": v(-69.91, -4.88) * mm});
            skLineSegment(sketch, "E119", {"start": v(-69.1, -3.69) * mm, "end": v(-69.1, -3.18) * mm});
            skLineSegment(sketch, "E120", {"start": v(-68.72, -3.4) * mm, "end": v(-69.1, -3.69) * mm});
            skLineSegment(sketch, "E121", {"start": v(-69.07, -3.82) * mm, "end": v(-68.65, -3.5) * mm});
            skLineSegment(sketch, "E122", {"start": v(-68.45, -4.65) * mm, "end": v(-69.07, -3.82) * mm});
            skLineSegment(sketch, "E123", {"start": v(-68.54, -4.72) * mm, "end": v(-68.45, -4.65) * mm});
            skLineSegment(sketch, "E124", {"start": v(-69.15, -3.91) * mm, "end": v(-68.54, -4.72) * mm});
            skLineSegment(sketch, "E125", {"start": v(-69.81, -4.95) * mm, "end": v(-69.15, -3.91) * mm});
            skLineSegment(sketch, "E126", {"start": v(-69.1, -3.18) * mm, "end": v(-69.22, -3.18) * mm});
            skLineSegment(sketch, "E127", {"start": v(-68.65, -3.5) * mm, "end": v(-68.72, -3.4) * mm});
            skCircle(sketch, "E128", {"center": v(-72.2, -0.49) * mm, "radius": 0.6 * mm});
            skLineSegment(sketch, "E129", {"start": v(-72.74, -0.14) * mm, "end": v(-72.78, -0.06) * mm});
            skArc(sketch, "E130", {"start": v(-72.74, -0.14) * mm, "mid": v(-73.2, -1.1) * mm, "end": v(-72.58, -1.95) * mm});
            skArc(sketch, "E131", {"start": v(-71.84, -2.8) * mm, "mid": v(-72.12, -2.3) * mm, "end": v(-72.58, -1.95) * mm});
            skLineSegment(sketch, "E132", {"start": v(-68.55, -8.64) * mm, "end": v(-68.4, -8.3) * mm});
            skArc(sketch, "E133", {"start": v(-72.19, -2.9) * mm, "mid": v(-72.39, -2.52) * mm, "end": v(-72.72, -2.28) * mm});
            skArc(sketch, "E134", {"start": v(-72.19, -2.9) * mm, "mid": v(-70.8, -6.04) * mm, "end": v(-68.55, -8.64) * mm});
            skArc(sketch, "E135", {"start": v(-72.78, -0.06) * mm, "mid": v(-73.45, -1.19) * mm, "end": v(-72.72, -2.28) * mm});
            skArc(sketch, "E136", {"start": v(-71.84, -2.8) * mm, "mid": v(-70.53, -5.8) * mm, "end": v(-68.4, -8.3) * mm});
            skLineSegment(sketch, "E137", {"start": v(-60.9, 0.22) * mm, "end": v(-9.95, 0.22) * mm, "construction": true});
            skSolve(sketch);
        }
        {
            var Q0;
            Q0 = qSketchRegion(id + "F26", true);
            extrude(context, id + "F27", {"entities" : qUnion([Q0]), "operationType" : NewBodyOperationType.REMOVE, "depth" : 6.5 * mm, "offsetDistance" : 25 * mm});
        }
    });
